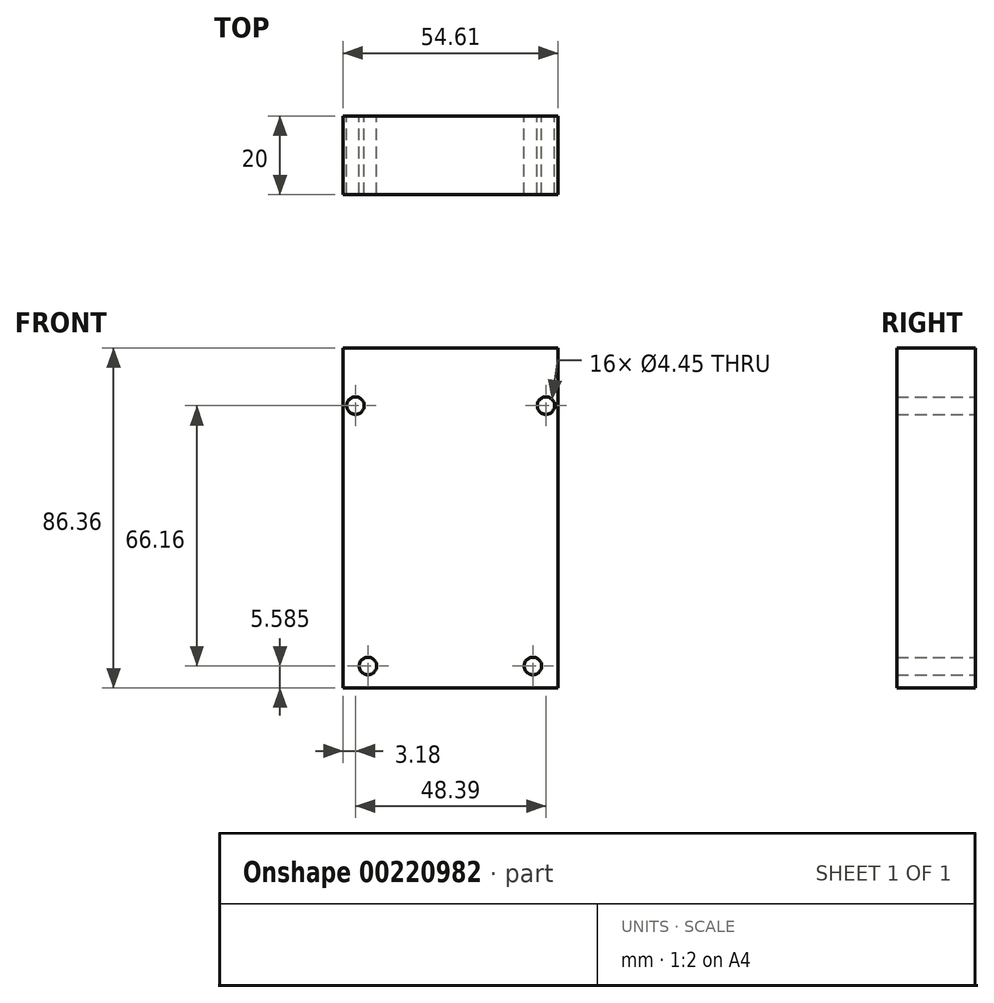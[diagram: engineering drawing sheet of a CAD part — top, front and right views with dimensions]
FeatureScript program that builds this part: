
annotation { "Feature Type Name" : "Feature", "Feature Type Description" : "" }
export const myFeature = defineFeature(function(context is Context, id is Id, definition is map)
    precondition{}
    {
        {
            var Q0;
            Q0=qCreatedBy(makeId("Front.planeOp"),FACE);
            var sketch = newSketch(context, id + "F0", { "sketchPlane" : qUnion([Q0])});
            skLineSegment(sketch, "E0", {"start": v(0, 42.9) * mm, "end": v(0, -43.45) * mm});
            skLineSegment(sketch, "E1", {"start": v(0, -43.45) * mm, "end": v(54.61, -43.45) * mm});
            skLineSegment(sketch, "E2", {"start": v(54.61, -43.45) * mm, "end": v(54.61, 42.9) * mm});
            skLineSegment(sketch, "E3", {"start": v(54.61, 42.9) * mm, "end": v(0, 42.9) * mm});
            skLineSegment(sketch, "E4", {"start": v(0, 42.9) * mm, "end": v(0, 28.3) * mm});
            skLineSegment(sketch, "E5", {"start": v(0, 28.3) * mm, "end": v(3.18, 28.3) * mm});
            skCircle(sketch, "E6", {"center": v(3.18, 28.3) * mm, "radius": 2.23 * mm});
            skLineSegment(sketch, "E7", {"start": v(0, -43.45) * mm, "end": v(0, -37.86) * mm});
            skLineSegment(sketch, "E8", {"start": v(0, -37.86) * mm, "end": v(6.35, -37.86) * mm});
            skCircle(sketch, "E9", {"center": v(6.35, -37.86) * mm, "radius": 2.22 * mm});
            skLineSegment(sketch, "E10", {"start": v(6.35, -37.86) * mm, "end": v(48.26, -37.86) * mm});
            skCircle(sketch, "E11", {"center": v(48.26, -37.86) * mm, "radius": 2.22 * mm});
            skLineSegment(sketch, "E12", {"start": v(3.18, 28.3) * mm, "end": v(51.57, 28.3) * mm});
            skCircle(sketch, "E13", {"center": v(51.57, 28.3) * mm, "radius": 2.23 * mm});
            skSolve(sketch);
        }
        {
            var Q0;
            Q0 = qSketchRegion(id + "F0", true);
            extrude(context, id + "F1", {"entities" : qUnion([Q0]), "depth" : 20 * mm, "offsetDistance" : 25 * mm});
        }
    });
